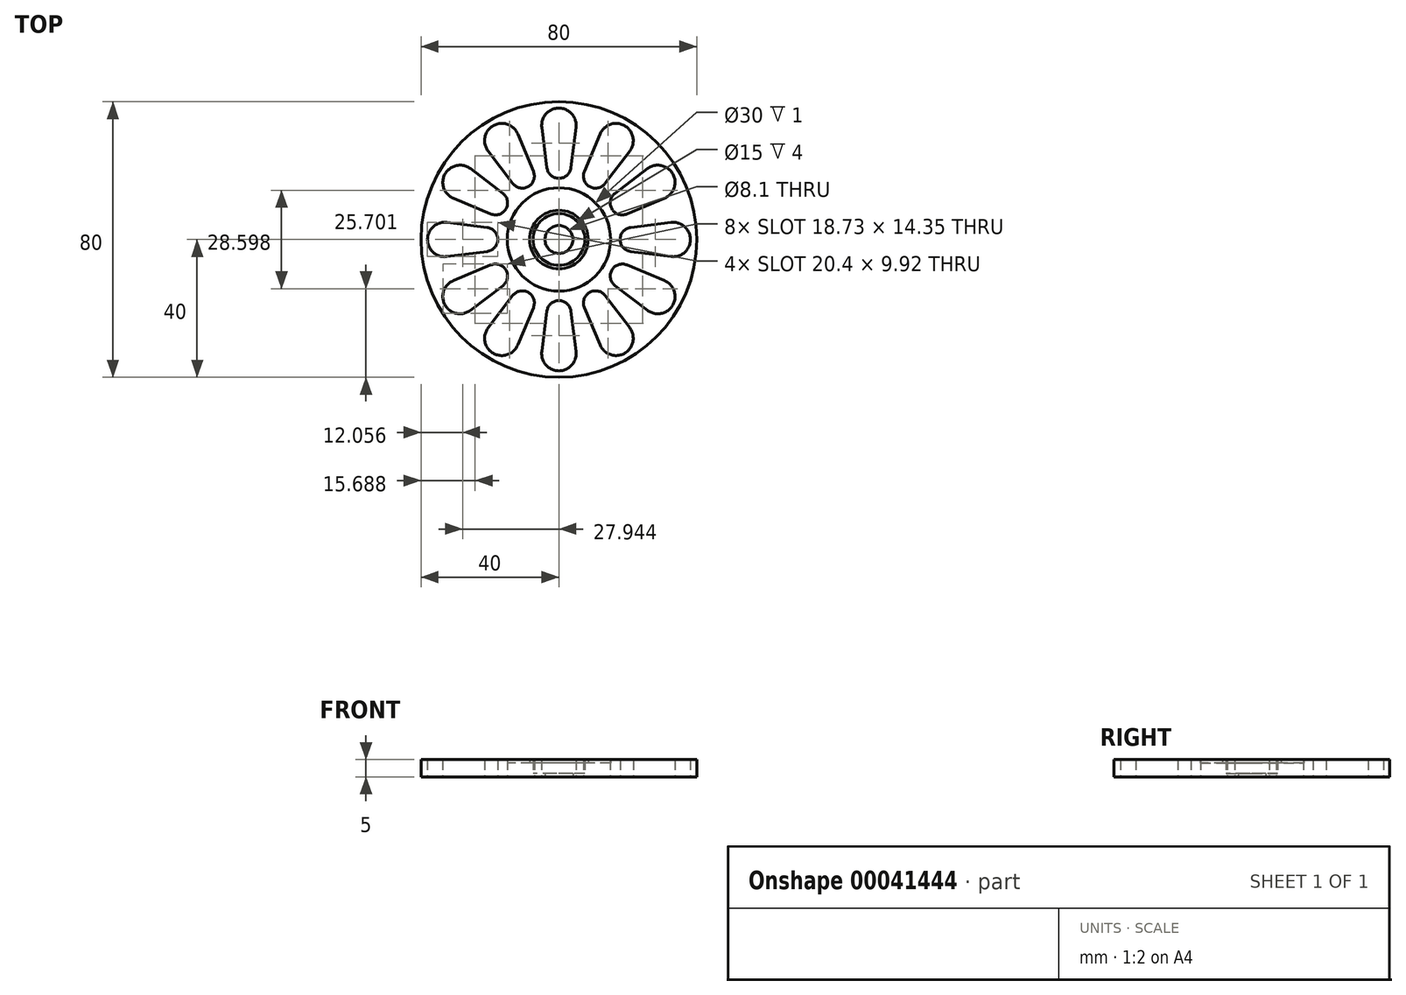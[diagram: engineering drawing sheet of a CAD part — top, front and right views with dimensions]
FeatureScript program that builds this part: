
annotation { "Feature Type Name" : "Feature", "Feature Type Description" : "" }
export const myFeature = defineFeature(function(context is Context, id is Id, definition is map)
    precondition{}
    {
        {
            var Q0;
            Q0=qCreatedBy(makeId("Top.planeOp"),FACE);
            var sketch = newSketch(context, id + "F0", { "sketchPlane" : qUnion([Q0])});
            skCircle(sketch, "E0", {"center": v(0, 0) * mm, "radius": 40 * mm});
            skCircle(sketch, "E1", {"center": v(0, 0) * mm, "radius": 8.5 * mm});
            skCircle(sketch, "E2", {"center": v(0, 0) * mm, "radius": 15 * mm});
            skArc(sketch, "E3", {"start": v(-3.47, 20.8) * mm, "mid": v(0, 17.74) * mm, "end": v(3.47, 20.8) * mm});
            skArc(sketch, "E4", {"start": v(4.96, 32.51) * mm, "mid": v(0, 38.14) * mm, "end": v(-4.96, 32.51) * mm});
            skLineSegment(sketch, "E5", {"start": v(-3.47, 20.8) * mm, "end": v(-4.96, 32.51) * mm});
            skLineSegment(sketch, "E6", {"start": v(4.96, 32.51) * mm, "end": v(3.47, 20.8) * mm});
            skArc(sketch, "E7.1.0", {"start": v(-11.96, 30.64) * mm, "mid": v(-19.07, 33.03) * mm, "end": v(-20.55, 25.68) * mm});
            skLineSegment(sketch, "E7.1.1", {"start": v(-13.4, 16.28) * mm, "end": v(-20.55, 25.68) * mm});
            skLineSegment(sketch, "E7.1.2", {"start": v(-11.96, 30.64) * mm, "end": v(-7.4, 19.75) * mm});
            skArc(sketch, "E7.1.3", {"start": v(-13.4, 16.28) * mm, "mid": v(-8.87, 15.37) * mm, "end": v(-7.4, 19.75) * mm});
            skArc(sketch, "E7.2.0", {"start": v(-25.68, 20.55) * mm, "mid": v(-33.03, 19.07) * mm, "end": v(-30.64, 11.96) * mm});
            skLineSegment(sketch, "E7.2.1", {"start": v(-19.75, 7.4) * mm, "end": v(-30.64, 11.96) * mm});
            skLineSegment(sketch, "E7.2.2", {"start": v(-25.68, 20.55) * mm, "end": v(-16.28, 13.4) * mm});
            skArc(sketch, "E7.2.3", {"start": v(-19.75, 7.4) * mm, "mid": v(-15.37, 8.87) * mm, "end": v(-16.28, 13.4) * mm});
            skArc(sketch, "E7.3.0", {"start": v(-32.51, 4.96) * mm, "mid": v(-38.14, 0) * mm, "end": v(-32.51, -4.96) * mm});
            skLineSegment(sketch, "E7.3.1", {"start": v(-20.8, -3.47) * mm, "end": v(-32.51, -4.96) * mm});
            skLineSegment(sketch, "E7.3.2", {"start": v(-32.51, 4.96) * mm, "end": v(-20.8, 3.47) * mm});
            skArc(sketch, "E7.3.3", {"start": v(-20.8, -3.47) * mm, "mid": v(-17.74, 0) * mm, "end": v(-20.8, 3.47) * mm});
            skArc(sketch, "E7.4.0", {"start": v(-30.64, -11.96) * mm, "mid": v(-33.03, -19.07) * mm, "end": v(-25.68, -20.55) * mm});
            skLineSegment(sketch, "E7.4.1", {"start": v(-16.28, -13.4) * mm, "end": v(-25.68, -20.55) * mm});
            skLineSegment(sketch, "E7.4.2", {"start": v(-30.64, -11.96) * mm, "end": v(-19.75, -7.4) * mm});
            skArc(sketch, "E7.4.3", {"start": v(-16.28, -13.4) * mm, "mid": v(-15.37, -8.87) * mm, "end": v(-19.75, -7.4) * mm});
            skArc(sketch, "E7.5.0", {"start": v(-20.55, -25.68) * mm, "mid": v(-19.07, -33.03) * mm, "end": v(-11.96, -30.64) * mm});
            skLineSegment(sketch, "E7.5.1", {"start": v(-7.4, -19.75) * mm, "end": v(-11.96, -30.64) * mm});
            skLineSegment(sketch, "E7.5.2", {"start": v(-20.55, -25.68) * mm, "end": v(-13.4, -16.28) * mm});
            skArc(sketch, "E7.5.3", {"start": v(-7.4, -19.75) * mm, "mid": v(-8.87, -15.37) * mm, "end": v(-13.4, -16.28) * mm});
            skArc(sketch, "E7.6.0", {"start": v(-4.96, -32.51) * mm, "mid": v(0, -38.14) * mm, "end": v(4.96, -32.51) * mm});
            skLineSegment(sketch, "E7.6.1", {"start": v(3.47, -20.8) * mm, "end": v(4.96, -32.51) * mm});
            skLineSegment(sketch, "E7.6.2", {"start": v(-4.96, -32.51) * mm, "end": v(-3.47, -20.8) * mm});
            skArc(sketch, "E7.6.3", {"start": v(3.47, -20.8) * mm, "mid": v(0, -17.74) * mm, "end": v(-3.47, -20.8) * mm});
            skArc(sketch, "E7.7.0", {"start": v(11.96, -30.64) * mm, "mid": v(19.07, -33.03) * mm, "end": v(20.55, -25.68) * mm});
            skLineSegment(sketch, "E7.7.1", {"start": v(13.4, -16.28) * mm, "end": v(20.55, -25.68) * mm});
            skLineSegment(sketch, "E7.7.2", {"start": v(11.96, -30.64) * mm, "end": v(7.4, -19.75) * mm});
            skArc(sketch, "E7.7.3", {"start": v(13.4, -16.28) * mm, "mid": v(8.87, -15.37) * mm, "end": v(7.4, -19.75) * mm});
            skArc(sketch, "E7.8.0", {"start": v(25.68, -20.55) * mm, "mid": v(33.03, -19.07) * mm, "end": v(30.64, -11.96) * mm});
            skLineSegment(sketch, "E7.8.1", {"start": v(19.75, -7.4) * mm, "end": v(30.64, -11.96) * mm});
            skLineSegment(sketch, "E7.8.2", {"start": v(25.68, -20.55) * mm, "end": v(16.28, -13.4) * mm});
            skArc(sketch, "E7.8.3", {"start": v(19.75, -7.4) * mm, "mid": v(15.37, -8.87) * mm, "end": v(16.28, -13.4) * mm});
            skArc(sketch, "E7.9.0", {"start": v(32.51, -4.96) * mm, "mid": v(38.14, 0) * mm, "end": v(32.51, 4.96) * mm});
            skLineSegment(sketch, "E7.9.1", {"start": v(20.8, 3.47) * mm, "end": v(32.51, 4.96) * mm});
            skLineSegment(sketch, "E7.9.2", {"start": v(32.51, -4.96) * mm, "end": v(20.8, -3.47) * mm});
            skArc(sketch, "E7.9.3", {"start": v(20.8, 3.47) * mm, "mid": v(17.74, 0) * mm, "end": v(20.8, -3.47) * mm});
            skArc(sketch, "E7.10.0", {"start": v(30.64, 11.96) * mm, "mid": v(33.03, 19.07) * mm, "end": v(25.68, 20.55) * mm});
            skLineSegment(sketch, "E7.10.1", {"start": v(16.28, 13.4) * mm, "end": v(25.68, 20.55) * mm});
            skLineSegment(sketch, "E7.10.2", {"start": v(30.64, 11.96) * mm, "end": v(19.75, 7.4) * mm});
            skArc(sketch, "E7.10.3", {"start": v(16.28, 13.4) * mm, "mid": v(15.37, 8.87) * mm, "end": v(19.75, 7.4) * mm});
            skArc(sketch, "E7.11.0", {"start": v(20.55, 25.68) * mm, "mid": v(19.07, 33.03) * mm, "end": v(11.96, 30.64) * mm});
            skLineSegment(sketch, "E7.11.1", {"start": v(7.4, 19.75) * mm, "end": v(11.96, 30.64) * mm});
            skLineSegment(sketch, "E7.11.2", {"start": v(20.55, 25.68) * mm, "end": v(13.4, 16.28) * mm});
            skArc(sketch, "E7.11.3", {"start": v(7.4, 19.75) * mm, "mid": v(8.87, 15.37) * mm, "end": v(13.4, 16.28) * mm});
            skCircle(sketch, "E8", {"center": v(0, 0) * mm, "radius": 7.5 * mm});
            skCircle(sketch, "E9", {"center": v(0, 0) * mm, "radius": 4.05 * mm});
            skSolve(sketch);
        }
        {
            var Q0;
            Q0=makeQuery(id+"F0.imprint","IMPRINT",FACE,{"disambiguationData":[TD([[makeQuery(id+"F0.imprint","IMPRINT",EDGE,{"derivedFrom":sQuery(id+"F0.wireOp",EDGE,"E0")}),1.0]])]});
            extrude(context, id + "F1", {"entities" : qUnion([Q0]), "depth" : 5 * mm});
        }
        {
            var Q0;
            Q0=makeQuery(id+"F0.imprint","IMPRINT",FACE,{"disambiguationData":[TD([[makeQuery(id+"F0.imprint","IMPRINT",EDGE,{"derivedFrom":sQuery(id+"F0.wireOp",EDGE,"E1")}),-1.0]])]});
            extrude(context, id + "F2", {"entities" : qUnion([Q0]), "operationType" : NewBodyOperationType.ADD, "depth" : 4 * mm});
        }
        {
            var Q0;
            Q0=makeQuery(id+"F0.imprint","IMPRINT",FACE,{"disambiguationData":[TD([[makeQuery(id+"F0.imprint","IMPRINT",EDGE,{"derivedFrom":sQuery(id+"F0.wireOp",EDGE,"E1")}),1.0]])]});
            extrude(context, id + "F3", {"entities" : qUnion([Q0]), "operationType" : NewBodyOperationType.ADD, "depth" : 5 * mm});
        }
        {
            var Q0;
            Q0=makeQuery(id+"F0.imprint","IMPRINT",FACE,{"disambiguationData":[TD([[makeQuery(id+"F0.imprint","IMPRINT",EDGE,{"derivedFrom":sQuery(id+"F0.wireOp",EDGE,"E8")}),1.0]])]});
            extrude(context, id + "F4", {"entities" : qUnion([Q0]), "operationType" : NewBodyOperationType.ADD, "depth" : 1 * mm});
        }
    });
